# Revit family: Basin-Inset-Fowler Contura Freeform1
name_source: partatom
category: Plumbing Fixtures
revit_build: Autodesk Revit Architecture 2012 (Build: 20110916_2132(x64)
units: mm (PartAtom-declared; Revit-internal decimal feet)

## types (1)
- Contura Freeform Inset
    Assembly Code = D2010310
    CW Connection = No
    Cost = 0 $
    Default Elevation = 0 mm  [stored 0 ft]
    Description = Contura Freeform Inset Basin
    HW Connection = No
    Keynote = WB
    Manufacturer = Fowler
    Material_ANZRS = Porcelain-White-Caroma
    Model = 895500W
    ModifiedIssue_ANZRS = 1.1 $
    Type Comments = Overflow not available, White plug and chrome flush fitting waste included
    URL = http://www.fowler.com.au
    Vent Connection = No
    WFU = 2
    Waste = Metal-Chrome-Caroma
    Waste Connection = Yes

note: [stored X ft] marks values corroborated as IEEE doubles in the binary element streams (Revit-internal decimal feet)

## geometry (parser evidence)
native form markers: Blend x2, Sweep x1
no freeform markers — native parametric forms only
